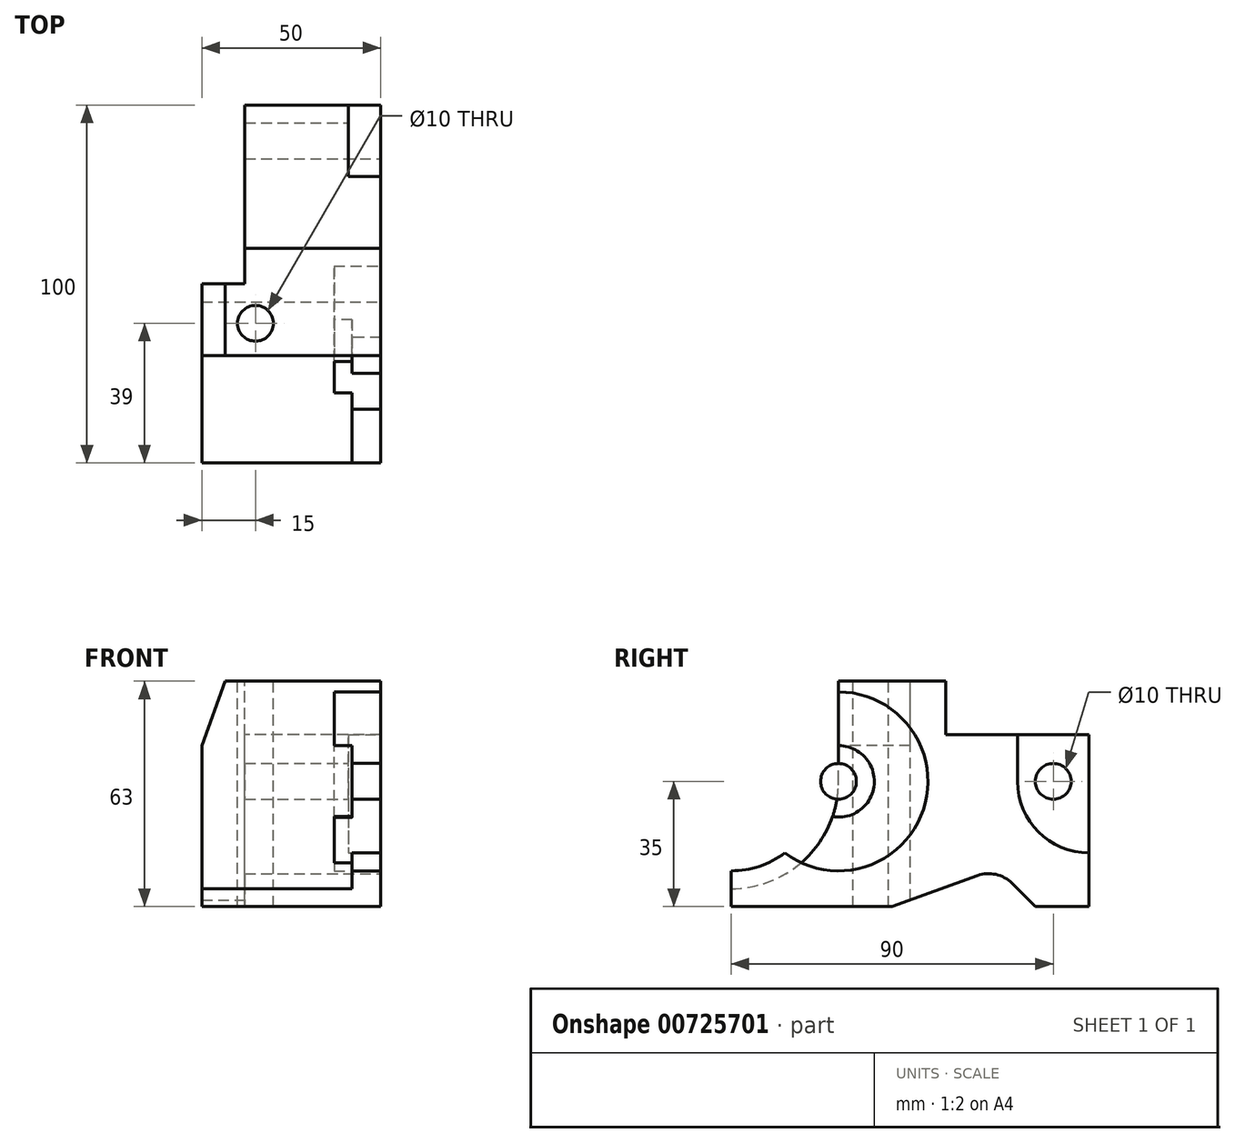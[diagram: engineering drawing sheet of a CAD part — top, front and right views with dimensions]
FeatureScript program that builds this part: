
annotation { "Feature Type Name" : "Feature", "Feature Type Description" : "" }
export const myFeature = defineFeature(function(context is Context, id is Id, definition is map)
    precondition{}
    {
        {
            var Q0;
            Q0=qCreatedBy(makeId("Right.planeOp"),FACE);
            var sketch = newSketch(context, id + "F0", { "sketchPlane" : qUnion([Q0])});
            skLineSegment(sketch, "E0.bottom", {"start": v(-50, 31.5) * mm, "end": v(50, 31.5) * mm});
            skLineSegment(sketch, "E0.top", {"start": v(-50, -31.5) * mm, "end": v(50, -31.5) * mm});
            skLineSegment(sketch, "E0.left", {"start": v(-50, 31.5) * mm, "end": v(-50, -31.5) * mm});
            skLineSegment(sketch, "E0.right", {"start": v(50, 31.5) * mm, "end": v(50, -31.5) * mm});
            skPoint(sketch, "E0.middle", {"position": v(0, 0) * mm});
            skSolve(sketch);
        }
        {
            var Q0;
            Q0 = qSketchRegion(id + "F0", true);
            extrude(context, id + "F1", {"entities" : qUnion([Q0]), "endBound" : BoundingType.SYMMETRIC, "depth" : 50 * mm, "offsetDistance" : 25 * mm});
        }
        {
            var Q0;
            Q0=makeQuery(id+"F1.opExtrude","SWEPT_FACE",FACE,{"disambiguationData":[OSD([sQuery(id+"F0.wireOp",EDGE,"E0.bottom")])]});
            var sketch = newSketch(context, id + "F2", { "sketchPlane" : qUnion([Q0])});
            skLineSegment(sketch, "E1", {"start": v(-25, 50) * mm, "end": v(25, 50) * mm});
            skLineSegment(sketch, "E2", {"start": v(25, 50) * mm, "end": v(25, 10) * mm});
            skLineSegment(sketch, "E3", {"start": v(25, 10) * mm, "end": v(-13, 10) * mm});
            skLineSegment(sketch, "E4", {"start": v(-13, 10) * mm, "end": v(-13, 0) * mm});
            skLineSegment(sketch, "E5", {"start": v(-13, 0) * mm, "end": v(-25, 0) * mm});
            skLineSegment(sketch, "E6", {"start": v(-25, 0) * mm, "end": v(-25, 50) * mm});
            skSolve(sketch);
        }
        {
            var Q0;
            Q0 = qSketchRegion(id + "F2", true);
            extrude(context, id + "F3", {"entities" : qUnion([Q0]), "operationType" : NewBodyOperationType.REMOVE, "oppositeDirection" : true, "depth" : 15 * mm, "offsetDistance" : 25 * mm});
        }
        {
            var Q0;
            Q0=makeQuery(id+"F1.opExtrude","CAP_FACE",FACE,{"disambiguationData":[OSD([sQuery(id+"F0.wireOp",EDGE,"E0.bottom"),sQuery(id+"F0.wireOp",EDGE,"E0.top"),sQuery(id+"F0.wireOp",EDGE,"E0.left"),sQuery(id+"F0.wireOp",EDGE,"E0.right")])],"isStart":false});
            var sketch = newSketch(context, id + "F4", { "sketchPlane" : qUnion([Q0])});
            skArc(sketch, "E7", {"start": v(-35, -16.5) * mm, "mid": v(5, 3.5) * mm, "end": v(-35, 23.5) * mm});
            skArc(sketch, "E8", {"start": v(-35, 23.5) * mm, "mid": v(-75, 3.5) * mm, "end": v(-35, -16.5) * mm});
            skArc(sketch, "E9", {"start": v(50, -16.5) * mm, "mid": v(35.86, -10.64) * mm, "end": v(30, 3.5) * mm});
            skLineSegment(sketch, "E10", {"start": v(30, 3.5) * mm, "end": v(30, 16.5) * mm});
            skLineSegment(sketch, "E11", {"start": v(30, 16.5) * mm, "end": v(50, 16.5) * mm});
            skLineSegment(sketch, "E12", {"start": v(50, 16.5) * mm, "end": v(50, -16.5) * mm});
            skSolve(sketch);
        }
        {
            var Q0;
            Q0 = qSketchRegion(id + "F4", true);
            extrude(context, id + "F5", {"entities" : qUnion([Q0]), "operationType" : NewBodyOperationType.REMOVE, "oppositeDirection" : true, "depth" : 9 * mm, "offsetDistance" : 25 * mm});
        }
        {
            var Q0;
            Q0=makeQuery(id+"F5.boolean.opBoolean","COPY",FACE,{"derivedFrom":makeQuery(id+"F5.opExtrude","CAP_FACE",FACE,{"disambiguationData":[OSD([sQuery(id+"F4.wireOp",EDGE,"E7"),sQuery(id+"F4.wireOp",EDGE,"E8")])],"isStart":false})});
            var sketch = newSketch(context, id + "F6", { "sketchPlane" : qUnion([Q0])});
            skArc(sketch, "E13", {"start": v(-35, -16.5) * mm, "mid": v(5, 3.5) * mm, "end": v(-35, 23.5) * mm});
            skArc(sketch, "E14", {"start": v(-35, 23.5) * mm, "mid": v(-75, 3.5) * mm, "end": v(-35, -16.5) * mm});
            skSolve(sketch);
        }
        {
            var Q0;
            Q0 = qSketchRegion(id + "F6", true);
            extrude(context, id + "F7", {"entities" : qUnion([Q0]), "operationType" : NewBodyOperationType.REMOVE, "oppositeDirection" : true, "depth" : 4 * mm, "offsetDistance" : 25 * mm});
        }
        {
            var Q0;
            Q0=makeQuery(id+"F7.boolean.opBoolean","COPY",FACE,{"derivedFrom":makeQuery(id+"F7.opExtrude","CAP_FACE",FACE,{"disambiguationData":[OSD([sQuery(id+"F6.wireOp",EDGE,"E13"),sQuery(id+"F6.wireOp",EDGE,"E14")])],"isStart":false})});
            var sketch = newSketch(context, id + "F8", { "sketchPlane" : qUnion([Q0])});
            skCircle(sketch, "E15", {"center": v(-20, 3.5) * mm, "radius": 10 * mm});
            skSolve(sketch);
        }
        {
            var Q0;
            Q0 = qSketchRegion(id + "F8", true);
            extrude(context, id + "F9", {"entities" : qUnion([Q0]), "operationType" : NewBodyOperationType.ADD, "depth" : 5 * mm, "offsetDistance" : 25 * mm});
        }
        {
            var Q0;
            Q0=makeQuery(id+"F1.opExtrude","CAP_FACE",FACE,{"disambiguationData":[OSD([sQuery(id+"F0.wireOp",EDGE,"E0.bottom"),sQuery(id+"F0.wireOp",EDGE,"E0.top"),sQuery(id+"F0.wireOp",EDGE,"E0.left"),sQuery(id+"F0.wireOp",EDGE,"E0.right")])],"isStart":true});
            var sketch = newSketch(context, id + "F10", { "sketchPlane" : qUnion([Q0])});
            skArc(sketch, "E16", {"start": v(50, -26.5) * mm, "mid": v(28.79, -17.71) * mm, "end": v(20, 3.5) * mm});
            skLineSegment(sketch, "E17", {"start": v(20, 3.5) * mm, "end": v(20, 31.5) * mm});
            skLineSegment(sketch, "E18", {"start": v(20, 31.5) * mm, "end": v(50, 31.5) * mm});
            skLineSegment(sketch, "E19", {"start": v(50, 31.5) * mm, "end": v(50, -26.5) * mm});
            skSolve(sketch);
        }
        {
            var Q0;
            Q0 = qSketchRegion(id + "F10", true);
            var Q1;
            Q1=makeQuery(id+"F1.opExtrude","CAP_FACE",FACE,{"disambiguationData":[OSD([sQuery(id+"F0.wireOp",EDGE,"E0.bottom"),sQuery(id+"F0.wireOp",EDGE,"E0.top"),sQuery(id+"F0.wireOp",EDGE,"E0.left"),sQuery(id+"F0.wireOp",EDGE,"E0.right")])],"isStart":false});
            extrude(context, id + "F11", {"entities" : qUnion([Q0]), "operationType" : NewBodyOperationType.REMOVE, "endBound" : BoundingType.UP_TO_SURFACE, "oppositeDirection" : true, "depth" : 25 * mm, "endBoundEntityFace" : qUnion([Q1]), "hasOffset" : true, "offsetDistance" : 8 * mm});
        }
        {
            var Q0;
            Q0=makeQuery(id+"F1.opExtrude","SWEPT_FACE",FACE,{"disambiguationData":[OSD([sQuery(id+"F0.wireOp",EDGE,"E0.bottom")])]});
            var sketch = newSketch(context, id + "F12", { "sketchPlane" : qUnion([Q0])});
            skLineSegment(sketch, "E20.bottom", {"start": v(17, -20) * mm, "end": v(25, -20) * mm});
            skLineSegment(sketch, "E20.top", {"start": v(17, -50) * mm, "end": v(25, -50) * mm});
            skLineSegment(sketch, "E20.left", {"start": v(17, -20) * mm, "end": v(17, -50) * mm});
            skLineSegment(sketch, "E20.right", {"start": v(25, -20) * mm, "end": v(25, -50) * mm});
            skSolve(sketch);
        }
        {
            var Q0;
            Q0 = qSketchRegion(id + "F12", true);
            extrude(context, id + "F13", {"entities" : qUnion([Q0]), "operationType" : NewBodyOperationType.REMOVE, "oppositeDirection" : true, "depth" : 10 * mm, "offsetDistance" : 25 * mm});
        }
        {
            var Q0;
            Q0=makeQuery(id+"F9.opExtrude","CAP_FACE",FACE,{"disambiguationData":[OSD([sQuery(id+"F8.wireOp",EDGE,"E15")])],"isStart":false});
            var sketch = newSketch(context, id + "F14", { "sketchPlane" : qUnion([Q0])});
            skCircle(sketch, "E21", {"center": v(-20, 3.5) * mm, "radius": 5 * mm});
            skSolve(sketch);
        }
        {
            var Q0;
            Q0 = qSketchRegion(id + "F14", true);
            extrude(context, id + "F15", {"entities" : qUnion([Q0]), "operationType" : NewBodyOperationType.ADD, "depth" : 8 * mm, "offsetDistance" : 25 * mm});
        }
        {
            var Q0;
            Q0=makeQuery(id+"F1.opExtrude","CAP_FACE",FACE,{"disambiguationData":[OSD([sQuery(id+"F0.wireOp",EDGE,"E0.bottom"),sQuery(id+"F0.wireOp",EDGE,"E0.top"),sQuery(id+"F0.wireOp",EDGE,"E0.left"),sQuery(id+"F0.wireOp",EDGE,"E0.right")])],"isStart":false});
            var sketch = newSketch(context, id + "F16", { "sketchPlane" : qUnion([Q0])});
            skLineSegment(sketch, "E22", {"start": v(-5, -31.5) * mm, "end": v(18.8, -22.84) * mm});
            skArc(sketch, "E23", {"start": v(18.8, -22.84) * mm, "mid": v(23.96, -22.5) * mm, "end": v(28.48, -24.98) * mm});
            skPoint(sketch, "E24", {"position": v(0, -31.5) * mm});
            skLineSegment(sketch, "E25", {"start": v(28.48, -24.98) * mm, "end": v(35, -31.5) * mm});
            skLineSegment(sketch, "E26", {"start": v(35, -31.5) * mm, "end": v(-5, -31.5) * mm});
            skSolve(sketch);
        }
        {
            var Q0;
            Q0=makeQuery(id+"F16.imprint","IMPRINT",FACE,{"disambiguationData":[TD([[makeQuery(id+"F16.imprint","IMPRINT",EDGE,{"derivedFrom":sQuery(id+"F16.wireOp",EDGE,"E22")}),-1.0]])]});
            extrude(context, id + "F17", {"entities" : qUnion([Q0]), "operationType" : NewBodyOperationType.REMOVE, "endBound" : BoundingType.THROUGH_ALL, "oppositeDirection" : true, "depth" : 25 * mm, "offsetDistance" : 25 * mm});
        }
        {
            var Q0;
            Q0=makeQuery(id+"F13.boolean.opBoolean","MERGE",FACE,{"derivedFrom":[makeQuery(id+"F11.boolean.opBoolean","COPY",FACE,{"derivedFrom":makeQuery(id+"F11.opExtrude","SWEPT_FACE",FACE,{"disambiguationData":[OSD([sQuery(id+"F10.wireOp",EDGE,"E17")])]})}),makeQuery(id+"F13.opExtrude","SWEPT_FACE",FACE,{"disambiguationData":[OSD([sQuery(id+"F12.wireOp",EDGE,"E20.bottom")])]})]});
            var sketch = newSketch(context, id + "F18", { "sketchPlane" : qUnion([Q0])});
            skLineSegment(sketch, "E27", {"start": v(-25, 31.5) * mm, "end": v(-18.45, 31.5) * mm});
            skLineSegment(sketch, "E28", {"start": v(-18.45, 31.5) * mm, "end": v(-25, 13.5) * mm});
            skLineSegment(sketch, "E29", {"start": v(-25, 13.5) * mm, "end": v(-25, 31.5) * mm});
            skSolve(sketch);
        }
        {
            var Q0;
            Q0 = qSketchRegion(id + "F18", true);
            extrude(context, id + "F19", {"entities" : qUnion([Q0]), "operationType" : NewBodyOperationType.REMOVE, "endBound" : BoundingType.THROUGH_ALL, "oppositeDirection" : true, "depth" : 25 * mm, "offsetDistance" : 25 * mm});
        }
        {
            var Q0;
            Q0=makeQuery(id+"F5.boolean.opBoolean","COPY",FACE,{"derivedFrom":makeQuery(id+"F5.opExtrude","CAP_FACE",FACE,{"disambiguationData":[OSD([sQuery(id+"F4.wireOp",EDGE,"E9"),sQuery(id+"F4.wireOp",EDGE,"E10"),sQuery(id+"F4.wireOp",EDGE,"E11"),sQuery(id+"F4.wireOp",EDGE,"E12")])],"isStart":false})});
            var sketch = newSketch(context, id + "F20", { "sketchPlane" : qUnion([Q0])});
            skCircle(sketch, "E30", {"center": v(40, 3.5) * mm, "radius": 5 * mm});
            skSolve(sketch);
        }
        {
            var Q0;
            Q0 = qSketchRegion(id + "F20", true);
            extrude(context, id + "F21", {"entities" : qUnion([Q0]), "operationType" : NewBodyOperationType.REMOVE, "endBound" : BoundingType.THROUGH_ALL, "oppositeDirection" : true, "depth" : 25 * mm, "offsetDistance" : 25 * mm});
        }
        {
            var Q0;
            Q0=makeQuery(id+"F1.opExtrude","SWEPT_FACE",FACE,{"disambiguationData":[OSD([sQuery(id+"F0.wireOp",EDGE,"E0.bottom")])]});
            var sketch = newSketch(context, id + "F22", { "sketchPlane" : qUnion([Q0])});
            skCircle(sketch, "E31", {"center": v(-10, -11) * mm, "radius": 5 * mm});
            skSolve(sketch);
        }
        {
            var Q0;
            Q0=makeQuery(id+"F22.imprint","IMPRINT",FACE,{"disambiguationData":[TD([[makeQuery(id+"F22.imprint","IMPRINT",EDGE,{"derivedFrom":sQuery(id+"F22.wireOp",EDGE,"E31")}),1.0]])]});
            extrude(context, id + "F23", {"entities" : qUnion([Q0]), "operationType" : NewBodyOperationType.REMOVE, "endBound" : BoundingType.THROUGH_ALL, "oppositeDirection" : true, "depth" : 25 * mm, "offsetDistance" : 25 * mm});
        }
        {
            var Q0;
            Q0=makeQuery(id+"F3.boolean.opBoolean","COPY",FACE,{"derivedFrom":makeQuery(id+"F3.opExtrude","CAP_FACE",FACE,{"disambiguationData":[OSD([sQuery(id+"F2.wireOp",EDGE,"E1"),sQuery(id+"F2.wireOp",EDGE,"E2"),sQuery(id+"F2.wireOp",EDGE,"E3"),sQuery(id+"F2.wireOp",EDGE,"E4"),sQuery(id+"F2.wireOp",EDGE,"E5"),sQuery(id+"F2.wireOp",EDGE,"E6")])],"isStart":false})});
            var sketch = newSketch(context, id + "F24", { "sketchPlane" : qUnion([Q0])});
            skLineSegment(sketch, "E32.bottom", {"start": v(-13, 0) * mm, "end": v(-25, 0) * mm});
            skLineSegment(sketch, "E32.top", {"start": v(-13, 50) * mm, "end": v(-25, 50) * mm});
            skLineSegment(sketch, "E32.left", {"start": v(-13, 0) * mm, "end": v(-13, 50) * mm});
            skLineSegment(sketch, "E32.right", {"start": v(-25, 0) * mm, "end": v(-25, 50) * mm});
            skSolve(sketch);
        }
        {
            var Q0;
            Q0 = qSketchRegion(id + "F24", true);
            extrude(context, id + "F25", {"entities" : qUnion([Q0]), "operationType" : NewBodyOperationType.REMOVE, "endBound" : BoundingType.THROUGH_ALL, "oppositeDirection" : true, "depth" : 25 * mm, "offsetDistance" : 25 * mm});
        }
    });
